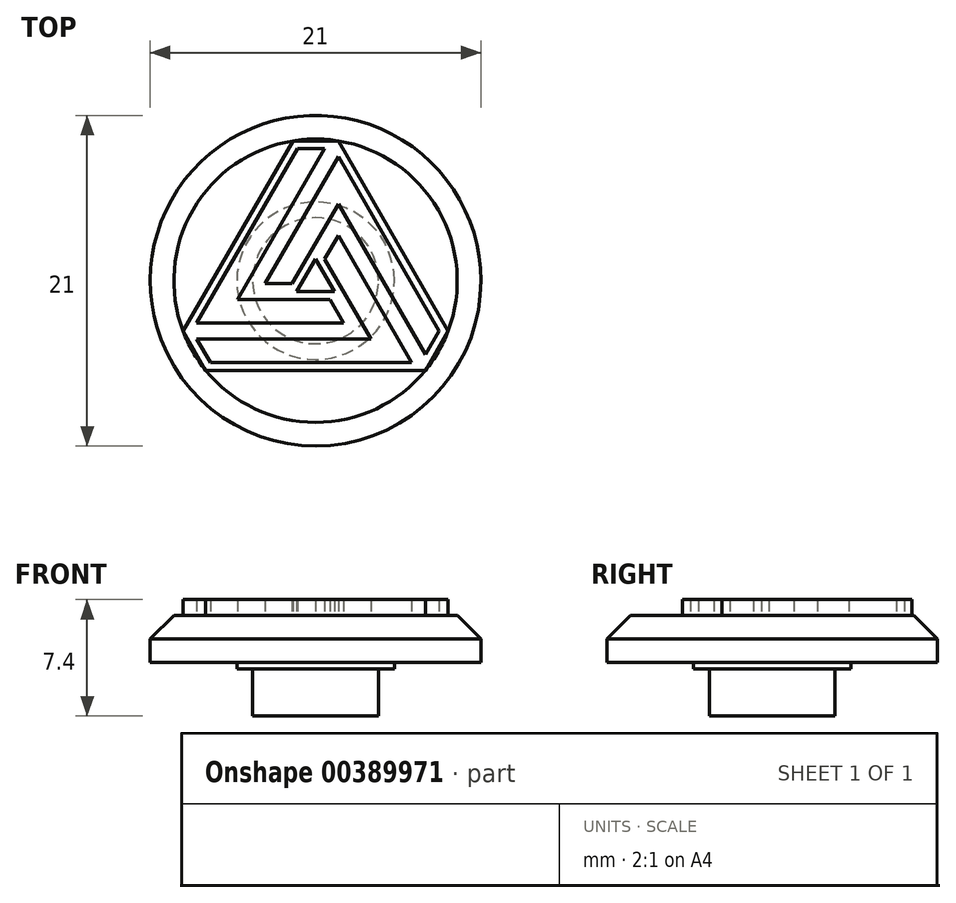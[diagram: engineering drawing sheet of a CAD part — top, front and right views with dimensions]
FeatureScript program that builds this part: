
annotation { "Feature Type Name" : "Feature", "Feature Type Description" : "" }
export const myFeature = defineFeature(function(context is Context, id is Id, definition is map)
    precondition{}
    {
        {
            var Q0;
            Q0=qCreatedBy(makeId("Right.planeOp"),FACE);
            var sketch = newSketch(context, id + "F0", { "sketchPlane" : qUnion([Q0])});
            skLineSegment(sketch, "E0", {"start": v(0, 0) * mm, "end": v(-4, 0) * mm});
            skLineSegment(sketch, "E1", {"start": v(-4, 0) * mm, "end": v(-4, 3) * mm});
            skLineSegment(sketch, "E2", {"start": v(-4, 3) * mm, "end": v(-5, 3) * mm});
            skLineSegment(sketch, "E3", {"start": v(-5, 3) * mm, "end": v(-5, 3.4) * mm});
            skLineSegment(sketch, "E4", {"start": v(-5, 3.4) * mm, "end": v(-10.5, 3.4) * mm});
            skLineSegment(sketch, "E5", {"start": v(-10.5, 3.4) * mm, "end": v(-10.5, 4.9) * mm});
            skLineSegment(sketch, "E6", {"start": v(-10.5, 4.9) * mm, "end": v(-9, 6.4) * mm});
            skLineSegment(sketch, "E7", {"start": v(-9, 6.4) * mm, "end": v(0, 6.4) * mm});
            skLineSegment(sketch, "E8", {"start": v(0, 6.4) * mm, "end": v(0, 0) * mm});
            skSolve(sketch);
        }
        {
            var Q0;
            Q0=makeQuery(id+"F0.imprint","IMPRINT",FACE,{"disambiguationData":[TD([[makeQuery(id+"F0.imprint","IMPRINT",EDGE,{"derivedFrom":sQuery(id+"F0.wireOp",EDGE,"E0")}),-1.0]])]});
            var Q1;
            Q1=sQuery(id+"F0.wireOp",EDGE,"E8");
            revolve(context, id + "F1", {"entities" : qUnion([Q0]), "axis" : qUnion([Q1]), "revolveType" : RevolveType.FULL});
        }
        {
            var Q0;
            Q0=makeQuery(id+"F1.opRevolve","SWEPT_FACE",FACE,{"disambiguationData":[OSD([sQuery(id+"F0.wireOp",EDGE,"E7")])]});
            var sketch = newSketch(context, id + "F2", { "sketchPlane" : qUnion([Q0])});
            skCircle(sketch, "E9.cCircle", {"center": v(0, 0) * mm, "radius": 11.38 * mm, "construction": true});
            skLineSegment(sketch, "E9.0", {"start": v(1.44, 8.88) * mm, "end": v(8.42, -3.2) * mm});
            skLineSegment(sketch, "E9.1", {"start": v(6.97, -5.7) * mm, "end": v(-6.97, -5.7) * mm});
            skLineSegment(sketch, "E9.2", {"start": v(-8.42, -3.2) * mm, "end": v(-1.44, 8.88) * mm});
            skCircle(sketch, "E10.cCircle", {"center": v(0, 0) * mm, "radius": 6.38 * mm, "construction": true});
            skLineSegment(sketch, "E10.0", {"start": v(1.44, 3.88) * mm, "end": v(6.97, -5.7) * mm});
            skLineSegment(sketch, "E10.1", {"start": v(2.64, -3.2) * mm, "end": v(-8.42, -3.2) * mm});
            skLineSegment(sketch, "E10.2", {"start": v(-4.08, -0.7) * mm, "end": v(1.44, 8.88) * mm});
            skCircle(sketch, "E11.cCircle", {"center": v(0, 0) * mm, "radius": 1.38 * mm, "construction": true});
            skLineSegment(sketch, "E11.0", {"start": v(0, 1.38) * mm, "end": v(1.2, -0.7) * mm});
            skLineSegment(sketch, "E11.1", {"start": v(1.2, -0.7) * mm, "end": v(-1.2, -0.7) * mm});
            skLineSegment(sketch, "E11.2", {"start": v(-1.2, -0.7) * mm, "end": v(0, 1.38) * mm});
            skLineSegment(sketch, "E12", {"start": v(-0.72, 0.13) * mm, "end": v(-2.89, 1.38) * mm, "construction": true});
            skLineSegment(sketch, "E13", {"start": v(-2.89, 1.38) * mm, "end": v(-5.05, 2.63) * mm, "construction": true});
            skLineSegment(sketch, "E14", {"start": v(0, 6.38) * mm, "end": v(1.44, 8.88) * mm, "construction": true});
            skLineSegment(sketch, "E15", {"start": v(0, 6.38) * mm, "end": v(-1.44, 8.88) * mm, "construction": true});
            skLineSegment(sketch, "E16", {"start": v(-1.44, 8.88) * mm, "end": v(1.44, 8.88) * mm});
            skLineSegment(sketch, "E17", {"start": v(8.42, -3.2) * mm, "end": v(6.97, -5.7) * mm});
            skLineSegment(sketch, "E18", {"start": v(-6.97, -5.7) * mm, "end": v(-8.42, -3.2) * mm});
            skLineSegment(sketch, "E19", {"start": v(1.2, -0.7) * mm, "end": v(2.64, -3.2) * mm});
            skLineSegment(sketch, "E20", {"start": v(-1.2, -0.7) * mm, "end": v(-4.08, -0.7) * mm});
            skLineSegment(sketch, "E21", {"start": v(0, 1.38) * mm, "end": v(1.44, 3.88) * mm});
            skPoint(sketch, "E22.orphan", {"position": v(5.53, -3.2) * mm});
            skPoint(sketch, "E23.orphan", {"position": v(-5.53, -3.2) * mm});
            skPoint(sketch, "E24.orphan", {"position": v(0, 11.38) * mm});
            skPoint(sketch, "E25.orphan", {"position": v(9.86, -5.7) * mm});
            skPoint(sketch, "E26.orphan", {"position": v(-9.86, -5.7) * mm});
            skLineSegment(sketch, "E27.0", {"start": v(1.78, -2.7) * mm, "end": v(-7.55, -2.7) * mm});
            skLineSegment(sketch, "E27.1", {"start": v(0.9, -1.2) * mm, "end": v(1.78, -2.7) * mm});
            skLineSegment(sketch, "E27.2", {"start": v(-1.15, 8.38) * mm, "end": v(0.58, 8.38) * mm});
            skLineSegment(sketch, "E27.3", {"start": v(-4.95, -1.2) * mm, "end": v(0.58, 8.38) * mm});
            skLineSegment(sketch, "E27.4", {"start": v(-1.2, -1.2) * mm, "end": v(-4.95, -1.2) * mm});
            skLineSegment(sketch, "E27.5", {"start": v(-7.55, -2.7) * mm, "end": v(-1.15, 8.38) * mm});
            skLineSegment(sketch, "E27.6", {"start": v(0.9, -1.2) * mm, "end": v(-1.2, -1.2) * mm});
            skLineSegment(sketch, "E28.0", {"start": v(-3.22, -0.2) * mm, "end": v(1.44, 7.88) * mm});
            skLineSegment(sketch, "E28.1", {"start": v(-1.49, -0.2) * mm, "end": v(-3.22, -0.2) * mm});
            skLineSegment(sketch, "E28.2", {"start": v(7.84, -3.2) * mm, "end": v(6.97, -4.7) * mm});
            skLineSegment(sketch, "E28.3", {"start": v(1.44, 4.88) * mm, "end": v(6.97, -4.7) * mm});
            skLineSegment(sketch, "E28.4", {"start": v(-0.43, 1.63) * mm, "end": v(1.44, 4.88) * mm});
            skLineSegment(sketch, "E28.5", {"start": v(1.44, 7.88) * mm, "end": v(7.84, -3.2) * mm});
            skLineSegment(sketch, "E28.6", {"start": v(-1.49, -0.2) * mm, "end": v(-0.43, 1.63) * mm});
            skLineSegment(sketch, "E29.0", {"start": v(1.63, -0.44) * mm, "end": v(3.5, -3.7) * mm});
            skLineSegment(sketch, "E29.1", {"start": v(0.58, 1.38) * mm, "end": v(1.63, -0.44) * mm});
            skLineSegment(sketch, "E29.2", {"start": v(-6.68, -5.2) * mm, "end": v(-7.55, -3.7) * mm});
            skLineSegment(sketch, "E29.3", {"start": v(6.1, -5.2) * mm, "end": v(-6.68, -5.2) * mm});
            skLineSegment(sketch, "E29.4", {"start": v(1.44, 2.88) * mm, "end": v(6.1, -5.2) * mm});
            skLineSegment(sketch, "E29.5", {"start": v(3.5, -3.7) * mm, "end": v(-7.55, -3.7) * mm});
            skLineSegment(sketch, "E29.6", {"start": v(0.58, 1.38) * mm, "end": v(1.44, 2.88) * mm});
            skSolve(sketch);
        }
        {
            var Q0;
            Q0=makeQuery(id+"F2.imprint","IMPRINT",FACE,{"disambiguationData":[TD([[makeQuery(id+"F2.imprint","IMPRINT",EDGE,{"derivedFrom":sQuery(id+"F2.wireOp",EDGE,"E9.1")}),-1.0]])]});
            var Q1;
            Q1=makeQuery(id+"F2.imprint","IMPRINT",FACE,{"disambiguationData":[TD([[makeQuery(id+"F2.imprint","IMPRINT",EDGE,{"derivedFrom":sQuery(id+"F2.wireOp",EDGE,"E9.2")}),-1.0]])]});
            var Q2;
            Q2=makeQuery(id+"F2.imprint","IMPRINT",FACE,{"disambiguationData":[TD([[makeQuery(id+"F2.imprint","IMPRINT",EDGE,{"derivedFrom":sQuery(id+"F2.wireOp",EDGE,"E9.0")}),-1.0]])]});
            extrude(context, id + "F3", {"entities" : qUnion([Q0, Q1, Q2]), "operationType" : NewBodyOperationType.ADD, "depth" : 1 * mm});
        }
    });
